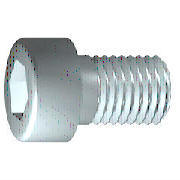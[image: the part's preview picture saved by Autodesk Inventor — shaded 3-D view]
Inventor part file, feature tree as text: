
AUTODESK INVENTOR PART (.ipt)
format: ipt  version: 2016 (Build 200138000, 138)  size: 199,680 bytes
history: native  units: mm (DEFAULTED — no unit token found)
features: sketch x2, extrude x1, plane x1, fillet x1
ambient origin geometry x7: Origin, YZ Plane, XY Plane, X Axis, Y Axis, Z Axis, Center Point
bodies: Solid1 (feature_tree), Body (feature_tree)
feature tree (5):
  extrude  "Slot"  Depth=5.0mm
  plane  "Work Plane1"
  fillet  "Fillet2"  Radius=5.0mm
  sketch  "Sketch1"  dims[d1=22.0mm d2=0.49086mm d3=5.0mm]
  sketch  "Sketch2"  dims[d4=2.5mm d5=60.0deg d6=5.0mm d7=5.0mm d8=4.618802mm d9=8.5mm d10=90.0deg d11=10.0mm d12=0.0mm d13=22.0mm d14=0.0mm d15=0.49076mm d16=0.49076mm d17=0.5mm d19=0.0mm d26=30.0mm d27=45.0deg d28=0.0mm d29=0.0mm d30=0.1mm]
